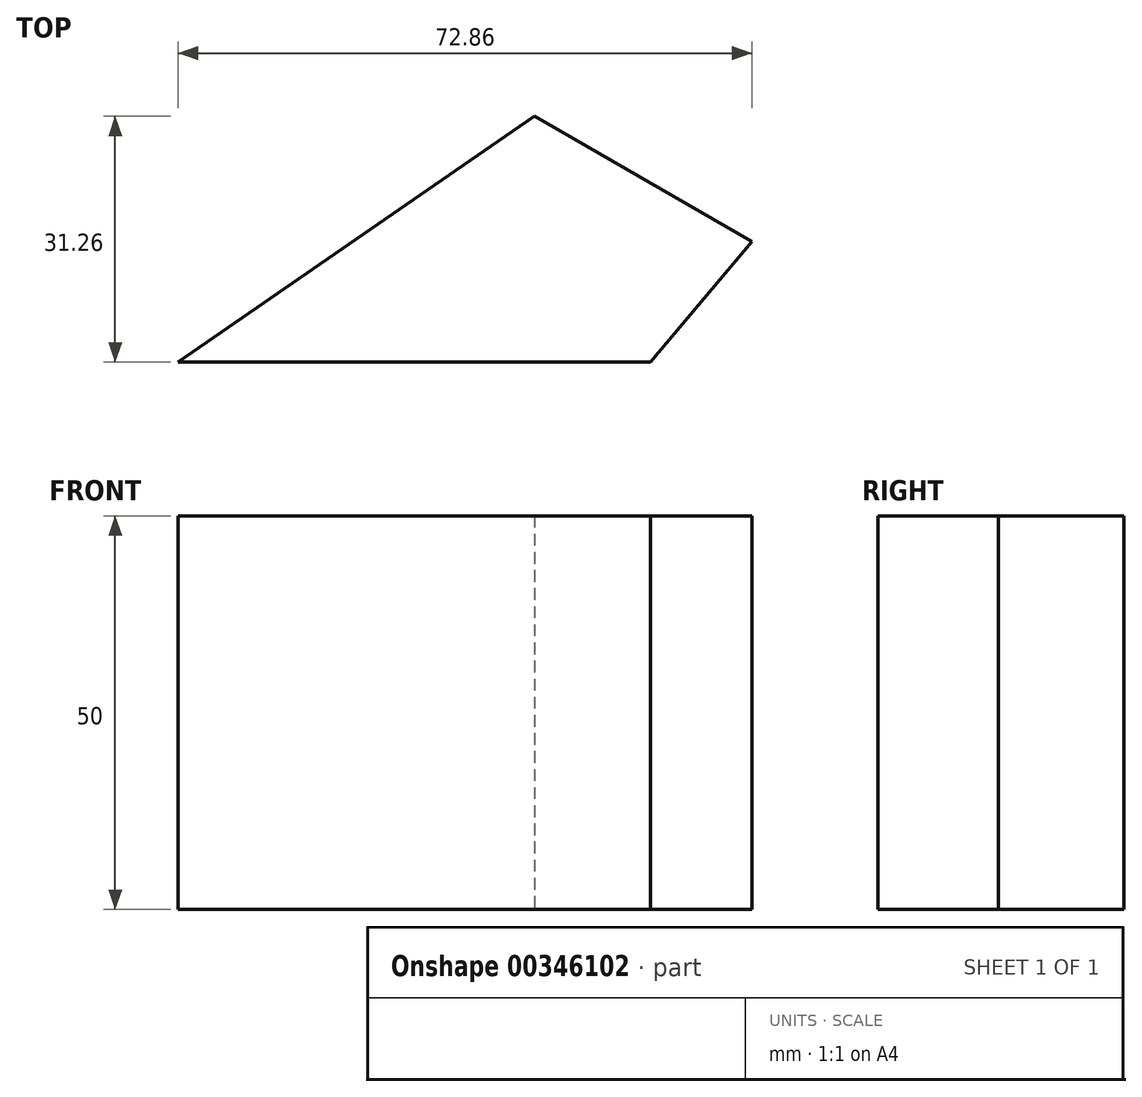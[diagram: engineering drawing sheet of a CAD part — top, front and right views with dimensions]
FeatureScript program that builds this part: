
annotation { "Feature Type Name" : "Feature", "Feature Type Description" : "" }
export const myFeature = defineFeature(function(context is Context, id is Id, definition is map)
    precondition{}
    {
        {
            var Q0;
            Q0=qCreatedBy(makeId("Top.planeOp"),FACE);
            var sketch = newSketch(context, id + "F0", { "sketchPlane" : qUnion([Q0])});
            skLineSegment(sketch, "E0", {"start": v(0, 0) * mm, "end": v(45.26, 31.26) * mm});
            skLineSegment(sketch, "E1", {"start": v(45.26, 31.26) * mm, "end": v(72.86, 15.32) * mm});
            skLineSegment(sketch, "E2", {"start": v(72.86, 15.32) * mm, "end": v(60, 0) * mm});
            skLineSegment(sketch, "E3", {"start": v(60, 0) * mm, "end": v(0, 0) * mm});
            skSolve(sketch);
        }
        {
            var Q0;
            Q0=makeQuery(id+"F0.imprint","IMPRINT",FACE,{"disambiguationData":[TD([[makeQuery(id+"F0.imprint","IMPRINT",EDGE,{"derivedFrom":sQuery(id+"F0.wireOp",EDGE,"E0")}),-1.0]])]});
            extrude(context, id + "F1", {"entities" : qUnion([Q0]), "endBound" : BoundingType.SYMMETRIC, "depth" : 50 * mm});
        }
    });
